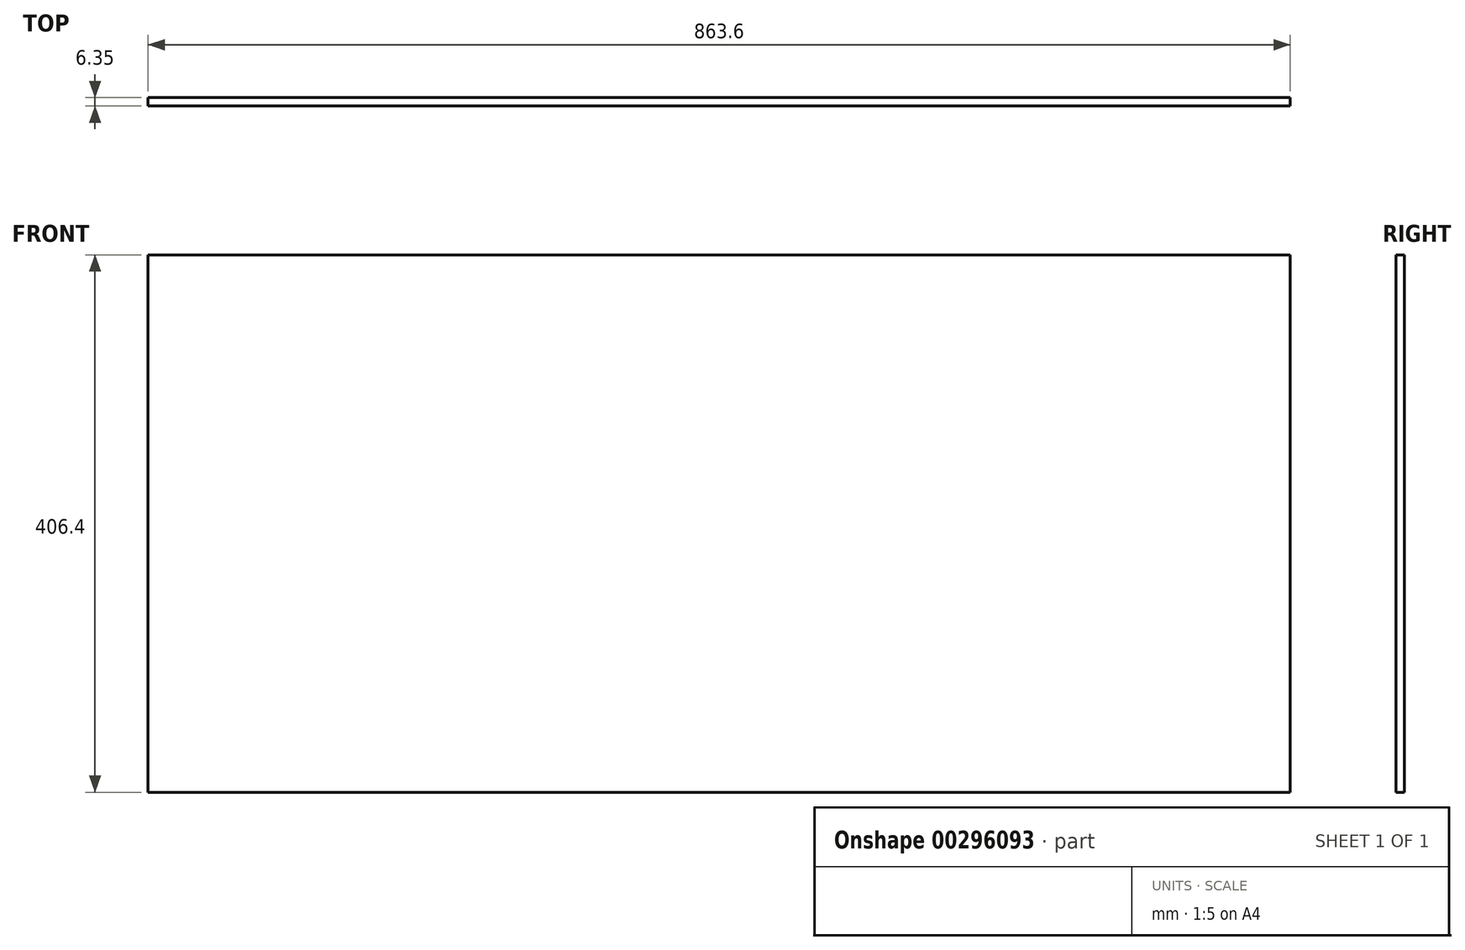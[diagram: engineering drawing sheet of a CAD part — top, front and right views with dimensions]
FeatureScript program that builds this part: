
annotation { "Feature Type Name" : "Feature", "Feature Type Description" : "" }
export const myFeature = defineFeature(function(context is Context, id is Id, definition is map)
    precondition{}
    {
        {
            var Q0;
            Q0=qCreatedBy(makeId("Front.planeOp"),FACE);
            var sketch = newSketch(context, id + "F0", { "sketchPlane" : qUnion([Q0])});
            skLineSegment(sketch, "E0.bottom", {"start": v(431.8, 203.2) * mm, "end": v(-431.8, 203.2) * mm});
            skLineSegment(sketch, "E0.top", {"start": v(431.8, -203.2) * mm, "end": v(-431.8, -203.2) * mm});
            skLineSegment(sketch, "E0.left", {"start": v(431.8, 203.2) * mm, "end": v(431.8, -203.2) * mm});
            skLineSegment(sketch, "E0.right", {"start": v(-431.8, 203.2) * mm, "end": v(-431.8, -203.2) * mm});
            skPoint(sketch, "E0.middle", {"position": v(0, 0) * mm});
            skSolve(sketch);
        }
        {
            var Q0;
            Q0=makeQuery(id+"F0.imprint","IMPRINT",FACE,{"disambiguationData":[TD([[makeQuery(id+"F0.imprint","IMPRINT",EDGE,{"derivedFrom":sQuery(id+"F0.wireOp",EDGE,"E0.bottom")}),1.0]])]});
            extrude(context, id + "F1", {"entities" : qUnion([Q0]), "depth" : 6.35 * mm});
        }
    });
